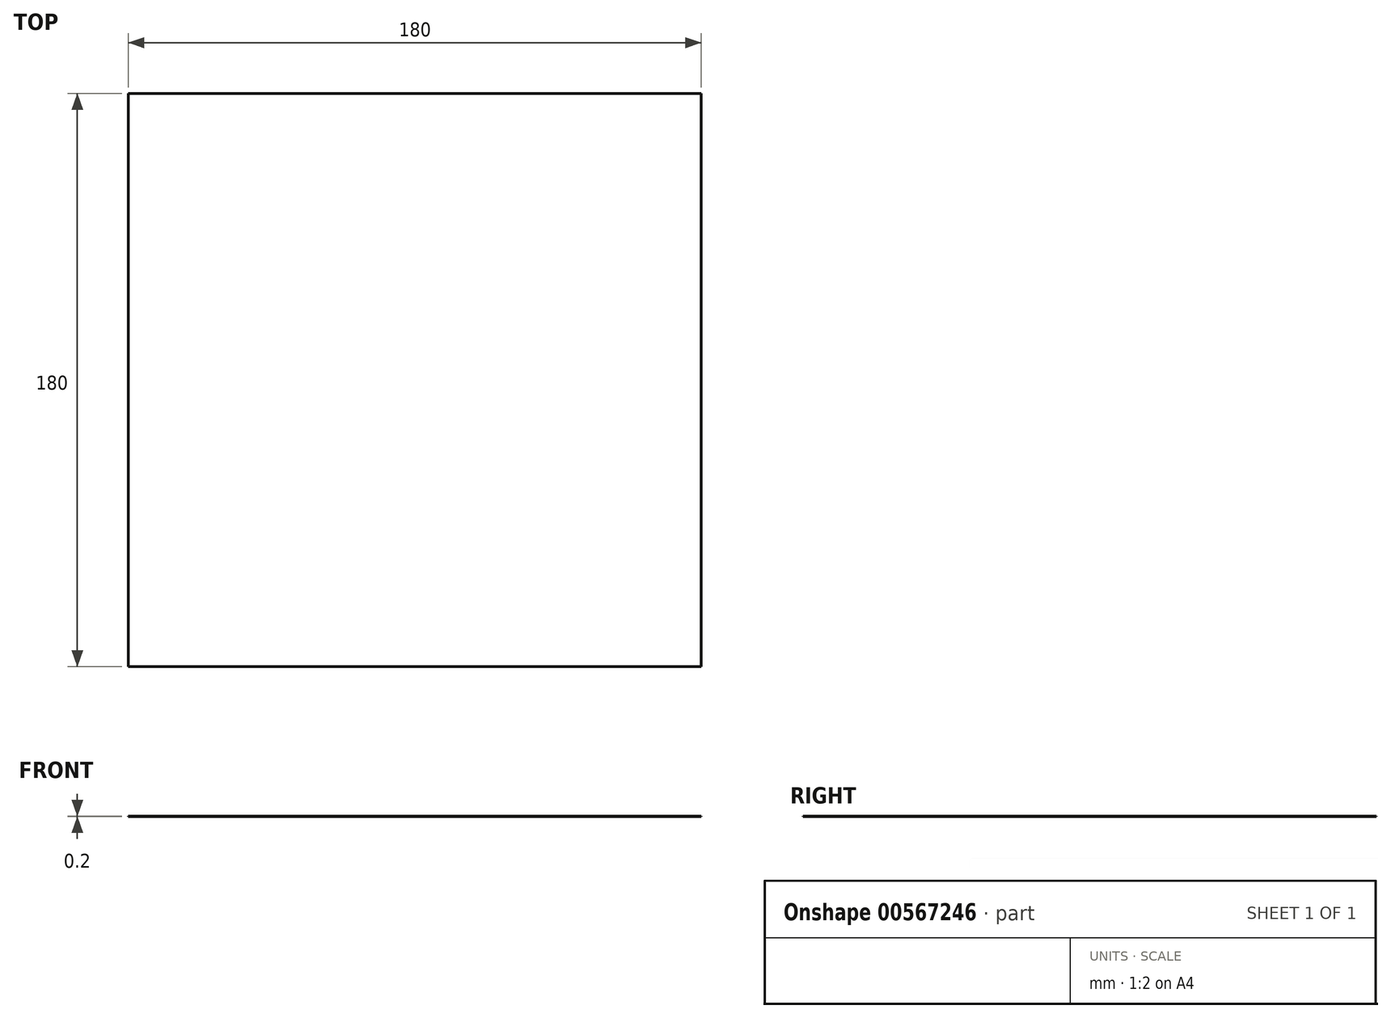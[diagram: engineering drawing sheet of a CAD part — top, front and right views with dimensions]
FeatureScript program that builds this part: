
annotation { "Feature Type Name" : "Feature", "Feature Type Description" : "" }
export const myFeature = defineFeature(function(context is Context, id is Id, definition is map)
    precondition{}
    {
        {
            var Q0;
            Q0=qCreatedBy(makeId("Top.planeOp"),FACE);
            var sketch = newSketch(context, id + "F0", { "sketchPlane" : qUnion([Q0])});
            skLineSegment(sketch, "E0.bottom", {"start": v(-206.87, 130.36) * mm, "end": v(-26.87, 130.36) * mm});
            skLineSegment(sketch, "E0.top", {"start": v(-206.87, -49.64) * mm, "end": v(-26.87, -49.64) * mm});
            skLineSegment(sketch, "E0.left", {"start": v(-206.87, 130.36) * mm, "end": v(-206.87, -49.64) * mm});
            skLineSegment(sketch, "E0.right", {"start": v(-26.87, 130.36) * mm, "end": v(-26.87, -49.64) * mm});
            skSolve(sketch);
        }
        {
            var Q0;
            Q0 = qSketchRegion(id + "F0", true);
            extrude(context, id + "F1", {"entities" : qUnion([Q0]), "depth" : 0.2 * mm, "offsetDistance" : 25 * mm});
        }
    });
